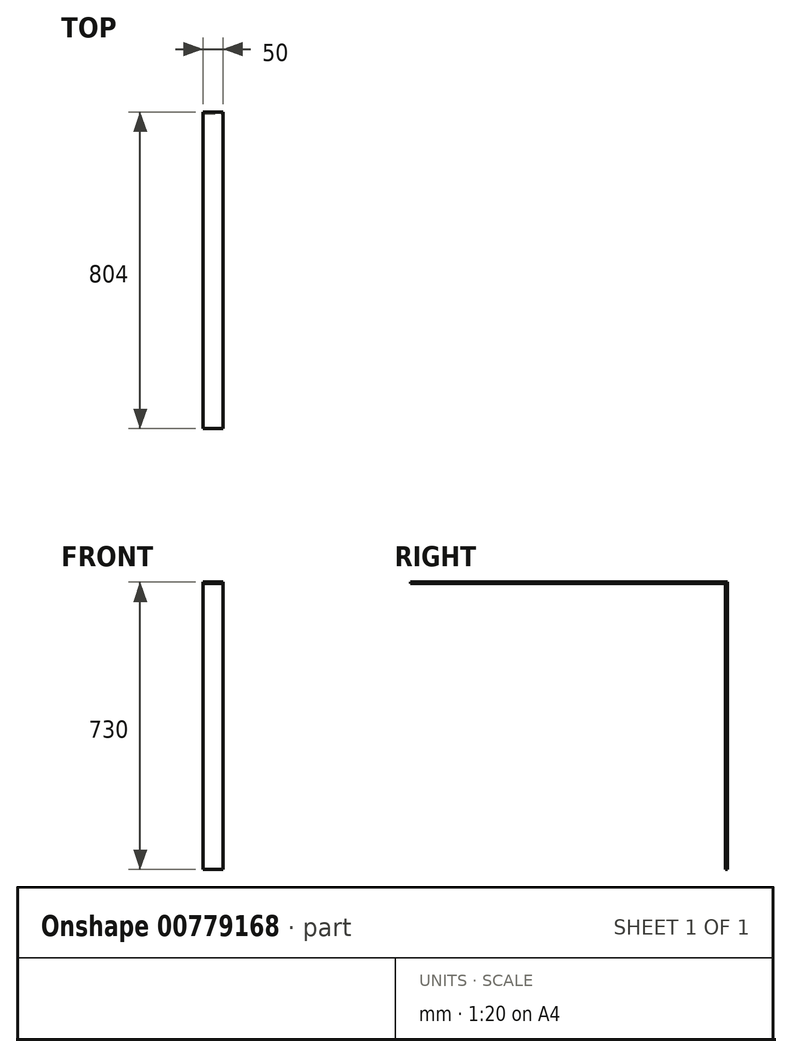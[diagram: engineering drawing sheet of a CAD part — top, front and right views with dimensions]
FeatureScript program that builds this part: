
annotation { "Feature Type Name" : "Feature", "Feature Type Description" : "" }
export const myFeature = defineFeature(function(context is Context, id is Id, definition is map)
    precondition{}
    {
        {
            var Q0;
            Q0=qCreatedBy(makeId("Front.planeOp"),FACE);
            var sketch = newSketch(context, id + "F0", { "sketchPlane" : qUnion([Q0])});
            skLineSegment(sketch, "E0", {"start": v(0, 0) * mm, "end": v(50, 0) * mm});
            skLineSegment(sketch, "E1", {"start": v(50, 0) * mm, "end": v(50, 4) * mm});
            skLineSegment(sketch, "E2", {"start": v(50, 4) * mm, "end": v(0, 4) * mm});
            skLineSegment(sketch, "E3", {"start": v(0, 4) * mm, "end": v(0, 0) * mm});
            skSolve(sketch);
        }
        {
            var Q0;
            Q0 = qSketchRegion(id + "F0", true);
            extrude(context, id + "F1", {"entities" : qUnion([Q0]), "depth" : 800 * mm, "offsetDistance" : 25 * mm});
        }
        {
            var Q0;
            Q0=qCreatedBy(makeId("Top.planeOp"),FACE);
            cPlane(context, id + "F2", {"entities" : qUnion([Q0]), "cplaneType" : CPlaneType.OFFSET, "offset" : 4 * mm, "width" : 150 * mm, "height" : 150 * mm});
        }
        {
            var Q0;
            Q0=qCreatedBy(id+"F2.planeOp",FACE);
            var sketch = newSketch(context, id + "F3", { "sketchPlane" : qUnion([Q0])});
            skLineSegment(sketch, "E4", {"start": v(0, 0) * mm, "end": v(50, 0) * mm});
            skLineSegment(sketch, "E5", {"start": v(50, 0) * mm, "end": v(50, 4) * mm});
            skLineSegment(sketch, "E6", {"start": v(50, 4) * mm, "end": v(0, 4) * mm});
            skLineSegment(sketch, "E7", {"start": v(0, 4) * mm, "end": v(0, 0) * mm});
            skSolve(sketch);
        }
        {
            var Q0;
            Q0 = qSketchRegion(id + "F3", true);
            extrude(context, id + "F4", {"entities" : qUnion([Q0]), "operationType" : NewBodyOperationType.ADD, "oppositeDirection" : true, "depth" : 730 * mm, "offsetDistance" : 25 * mm});
        }
    });
